# Revit family: Walls_Moving_walls_Komandor_MAW_110_without_door_Z1
name_source: partatom
category: Generic Models
revit_build: Autodesk Revit 2014 (Build: 20130308_1515(x64)
units: mm (PartAtom-declared; Revit-internal decimal feet)

## types (1)
- Walls_Moving_walls_Komandor_MAW_110_without_door_Z1
    1st Bar Distance = 2750 mm  [stored 9.02231 ft]
    2nd Bar Distance = 5500 mm  [stored 18.0446 ft]
    BIMobject category = Internal Walls
    COBIe Type Category = Wall DEMOUNTABLE
    Date of publishing = 12/1/2016
    Design country = Poland
    Edition number = 1
    IFC Classification = Wall
    Manufacturer country = Poland
    Manufacturer name = Komandor
    Masterformat 2014 Code = 09 70 00
    Masterformat 2014 Description = Wall Finishes
    Material main = Aluminium
    Material secondary = MDF
    NBS Reference Code = 25-30-20-80
    NBS Reference Description = Sliding Stacking Panel Partition Systems
    Nominal height = 0
    Nominal width = 0
    OmniClass Code = 23-15 13 19
    OmniClass Description = Wall Panels
    Panel Material = Veneer, LF-2
    Product Guid = 11ff6425-1177-4e66-8b54-3990dd030f65
    Product SKU = taw110
    Product data url = https://bimobject.com
    Product family = Walls
    Product group = TAW
    Profile Material = Komandor_Aluminum
    QR code = http://bimobject.com
    UNSPSC Code = 301615
    Uniclass 1.4 Code = L83122
    Uniclass 1.4 Description = Wall units
    Uniclass 2.0 Code = SS-25-30-20-80
    Uniclass 2.0 Description = Sliding Stacking Panel Partition Systems
    Uniclass 2015 Code = EF_25
    Uniclass 2015 Name = Wall and barrier elements
    Uniformat II Code = C3010
    Uniformat II Description = Wall Finishes
    Weight Net (Kg) = 0
    Youtube clip = https://www.youtube.com

note: [stored X ft] marks values corroborated as IEEE doubles in the binary element streams (Revit-internal decimal feet)

## geometry (parser evidence)
native form markers: Sweep x39
no freeform markers — native parametric forms only
